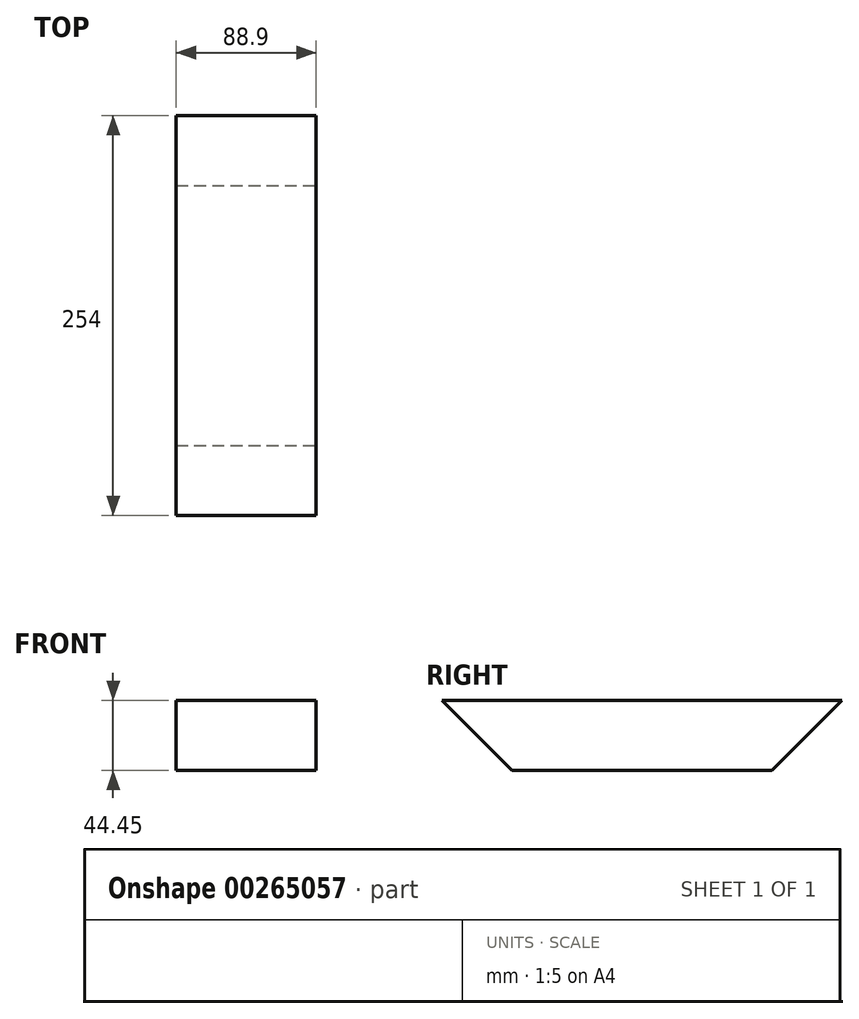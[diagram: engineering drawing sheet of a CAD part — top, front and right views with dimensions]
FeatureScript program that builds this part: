
annotation { "Feature Type Name" : "Feature", "Feature Type Description" : "" }
export const myFeature = defineFeature(function(context is Context, id is Id, definition is map)
    precondition{}
    {
        {
            var Q0;
            Q0=qCreatedBy(makeId("Front.planeOp"),FACE);
            var sketch = newSketch(context, id + "F0", { "sketchPlane" : qUnion([Q0])});
            skLineSegment(sketch, "E0.bottom", {"start": v(0, 0) * mm, "end": v(88.9, 0) * mm});
            skLineSegment(sketch, "E0.top", {"start": v(0, 44.45) * mm, "end": v(88.9, 44.45) * mm});
            skLineSegment(sketch, "E0.left", {"start": v(0, 0) * mm, "end": v(0, 44.45) * mm});
            skLineSegment(sketch, "E0.right", {"start": v(88.9, 0) * mm, "end": v(88.9, 44.45) * mm});
            skSolve(sketch);
        }
        {
            var Q0;
            Q0 = qSketchRegion(id + "F0", true);
            extrude(context, id + "F1", {"entities" : qUnion([Q0]), "depth" : 254 * mm});
        }
        {
            var Q0;
            Q0=makeQuery(id+"F1.opExtrude","SWEPT_FACE",FACE,{"disambiguationData":[OSD([sQuery(id+"F0.wireOp",EDGE,"E0.right")])]});
            var sketch = newSketch(context, id + "F2", { "sketchPlane" : qUnion([Q0])});
            skLineSegment(sketch, "E1", {"start": v(-254, 44.45) * mm, "end": v(-209.55, 0) * mm});
            skLineSegment(sketch, "E2", {"start": v(-209.55, 0) * mm, "end": v(-254, 0) * mm});
            skLineSegment(sketch, "E3", {"start": v(-254, 0) * mm, "end": v(-254, 44.45) * mm});
            skLineSegment(sketch, "E4", {"start": v(-127, -14.1) * mm, "end": v(-127, 54.55) * mm, "construction": true});
            skPoint(sketch, "E4.startSnap0", {"position": v(-127, 0) * mm});
            skLineSegment(sketch, "E5.MirrorCS", {"start": v(0, 44.45) * mm, "end": v(-44.45, 0) * mm});
            skLineSegment(sketch, "E6.MirrorCS", {"start": v(-44.45, 0) * mm, "end": v(0, 0) * mm});
            skLineSegment(sketch, "E7.MirrorCS", {"start": v(0, 0) * mm, "end": v(0, 44.45) * mm});
            skSolve(sketch);
        }
        {
            var Q0;
            Q0 = qSketchRegion(id + "F2", true);
            extrude(context, id + "F3", {"entities" : qUnion([Q0]), "operationType" : NewBodyOperationType.REMOVE, "oppositeDirection" : true, "depth" : 101.6 * mm});
        }
    });
